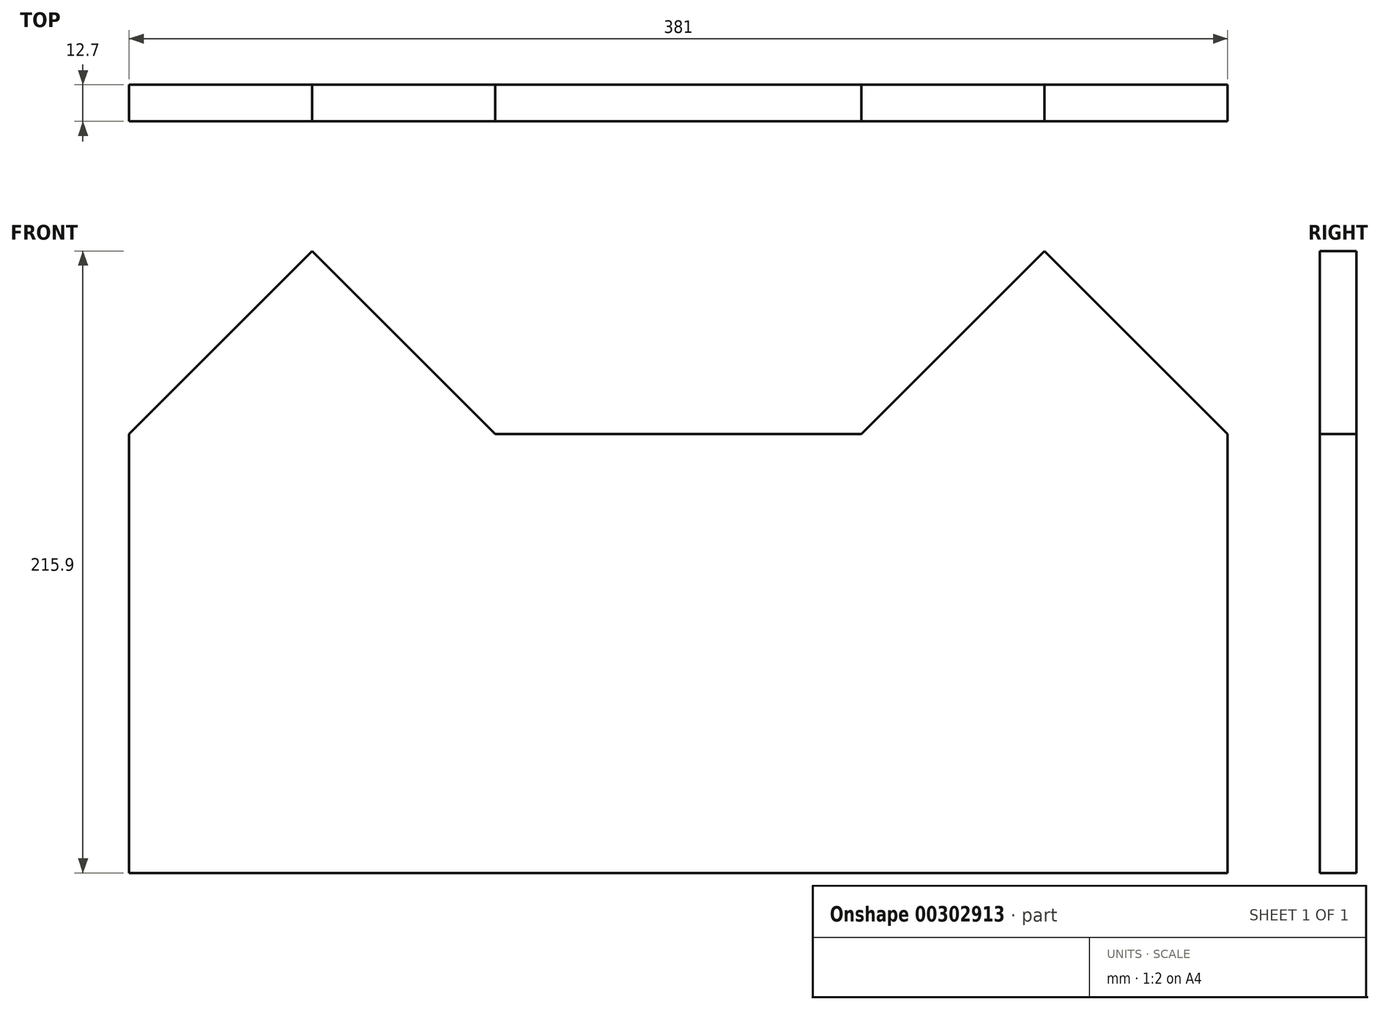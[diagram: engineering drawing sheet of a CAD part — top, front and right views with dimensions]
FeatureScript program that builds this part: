
annotation { "Feature Type Name" : "Feature", "Feature Type Description" : "" }
export const myFeature = defineFeature(function(context is Context, id is Id, definition is map)
    precondition{}
    {
        {
            var Q0;
            Q0=qCreatedBy(makeId("Front.planeOp"),FACE);
            var sketch = newSketch(context, id + "F0", { "sketchPlane" : qUnion([Q0])});
            skLineSegment(sketch, "E0.bottom", {"start": v(63.5, 76.2) * mm, "end": v(-63.5, 76.2) * mm, "construction": true});
            skLineSegment(sketch, "E0.top", {"start": v(63.5, -76.2) * mm, "end": v(-63.5, -76.2) * mm});
            skLineSegment(sketch, "E0.left", {"start": v(63.5, 76.2) * mm, "end": v(63.5, -76.2) * mm});
            skLineSegment(sketch, "E0.right", {"start": v(-63.5, 76.2) * mm, "end": v(-63.5, -76.2) * mm});
            skPoint(sketch, "E0.middle", {"position": v(0, 0) * mm});
            skLineSegment(sketch, "E1", {"start": v(-63.5, 76.2) * mm, "end": v(0, 139.7) * mm});
            skLineSegment(sketch, "E2", {"start": v(0, 139.7) * mm, "end": v(63.5, 76.2) * mm});
            skLineSegment(sketch, "E3", {"start": v(0, 139.7) * mm, "end": v(0, 76.2) * mm, "construction": true});
            skLineSegment(sketch, "E4.bottom", {"start": v(63.5, 76.2) * mm, "end": v(190.5, 76.2) * mm});
            skLineSegment(sketch, "E4.top", {"start": v(63.5, -76.2) * mm, "end": v(190.5, -76.2) * mm});
            skLineSegment(sketch, "E4.left", {"start": v(63.5, 76.2) * mm, "end": v(63.5, -76.2) * mm, "construction": true});
            skLineSegment(sketch, "E4.right", {"start": v(190.5, 76.2) * mm, "end": v(190.5, -76.2) * mm, "construction": true});
            skLineSegment(sketch, "E5.bottom", {"start": v(190.5, -76.2) * mm, "end": v(317.5, -76.2) * mm});
            skLineSegment(sketch, "E5.top", {"start": v(190.5, 76.2) * mm, "end": v(317.5, 76.2) * mm, "construction": true});
            skLineSegment(sketch, "E5.left", {"start": v(190.5, -76.2) * mm, "end": v(190.5, 76.2) * mm});
            skLineSegment(sketch, "E5.right", {"start": v(317.5, -76.2) * mm, "end": v(317.5, 76.2) * mm});
            skLineSegment(sketch, "E6", {"start": v(190.5, 76.2) * mm, "end": v(254, 139.7) * mm});
            skLineSegment(sketch, "E7", {"start": v(254, 139.7) * mm, "end": v(317.5, 76.2) * mm});
            skSolve(sketch);
        }
        {
            var Q0;
            Q0=makeQuery(id+"F0.imprint","IMPRINT",FACE,{"disambiguationData":[TD([[makeQuery(id+"F0.imprint","IMPRINT",EDGE,{"derivedFrom":sQuery(id+"F0.wireOp",EDGE,"E0.top")}),-1.0]])]});
            var Q1;
            Q1=makeQuery(id+"F0.imprint","IMPRINT",FACE,{"disambiguationData":[TD([[makeQuery(id+"F0.imprint","IMPRINT",EDGE,{"derivedFrom":sQuery(id+"F0.wireOp",EDGE,"E4.bottom")}),-1.0]])]});
            var Q2;
            Q2=makeQuery(id+"F0.imprint","IMPRINT",FACE,{"disambiguationData":[TD([[makeQuery(id+"F0.imprint","IMPRINT",EDGE,{"derivedFrom":sQuery(id+"F0.wireOp",EDGE,"E5.bottom")}),1.0]])]});
            var Q3;
            Q3=makeQuery(id+"F0.imprint","IMPRINT",FACE,{"disambiguationData":[TD([[makeQuery(id+"F0.imprint","IMPRINT",EDGE,{"derivedFrom":sQuery(id+"F0.wireOp",EDGE,"E5.top")}),1.0]])]});
            extrude(context, id + "F1", {"entities" : qUnion([Q0, Q1, Q2, Q3]), "depth" : 12.7 * mm});
        }
    });
